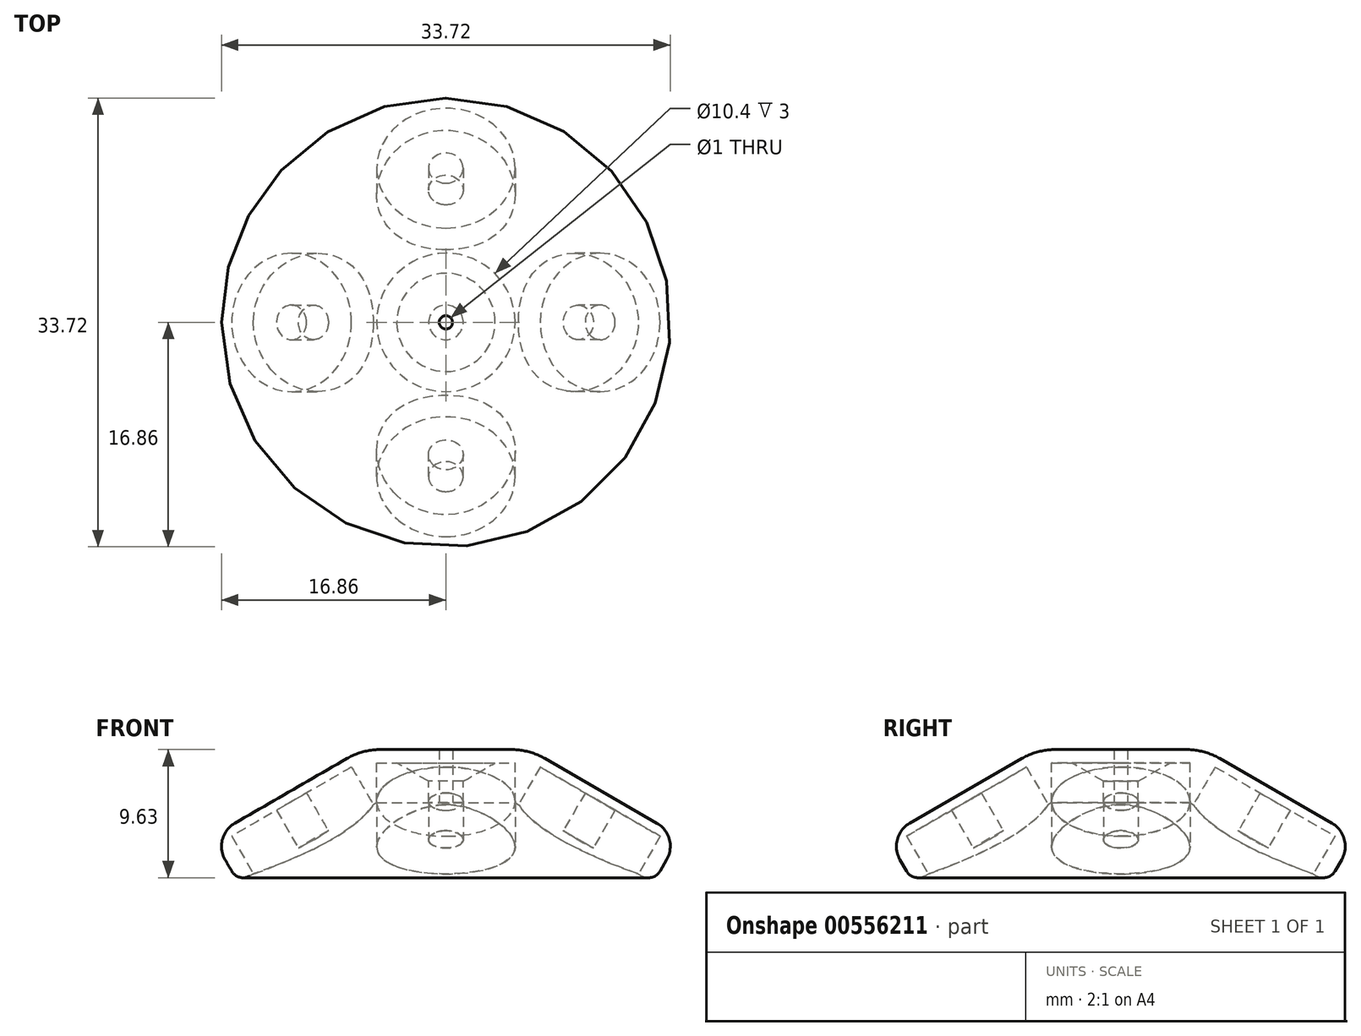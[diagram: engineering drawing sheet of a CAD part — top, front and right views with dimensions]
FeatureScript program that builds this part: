
annotation { "Feature Type Name" : "Feature", "Feature Type Description" : "" }
export const myFeature = defineFeature(function(context is Context, id is Id, definition is map)
    precondition{}
    {
        {
            var Q0;
            Q0=qCreatedBy(makeId("Top.planeOp"),FACE);
            var sketch = newSketch(context, id + "F0", { "sketchPlane" : qUnion([Q0])});
            skCircle(sketch, "E0", {"center": v(0, 0) * mm, "radius": 5 * mm});
            skSolve(sketch);
        }
        {
            var Q0;
            Q0=makeQuery(id+"F0.imprint","IMPRINT",FACE,{"disambiguationData":[TD([[makeQuery(id+"F0.imprint","IMPRINT",EDGE,{"derivedFrom":sQuery(id+"F0.wireOp",EDGE,"E0")}),1.0]])]});
            extrude(context, id + "F1", {"entities" : qUnion([Q0]), "depth" : 2.8 * mm, "offsetDistance" : 25 * mm});
        }
        {
            var Q0;
            Q0=sQuery(id+"F0.wireOp",VERTEX,"E0.center");
            var Q1;
            Q1=makeQuery(id+"F1.opExtrude","SWEPT_BODY",BODY,{"disambiguationData":[OSD([sQuery(id+"F0.wireOp",EDGE,"E0")])]});
            hole(context, id + "F2", {"style" : HoleStyle.C_SINK, "endStyle" : HoleEndStyle.THROUGH, "oppositeDirection" : true, "holeDiameter" : 3 * mm, "cSinkDiameter" : 7.5 * mm, "cSinkAngle" : 120 * degree, "isTappedThrough" : true, "tappedDepth" : 12 * mm, "tapClearance" : 3, "locations" : qUnion([Q0]), "scope" : qUnion([Q1])});
        }
        {
            var Q0;
            Q0=qCreatedBy(makeId("Front.planeOp"),FACE);
            var sketch = newSketch(context, id + "F3", { "sketchPlane" : qUnion([Q0])});
            skLineSegment(sketch, "E1", {"start": v(0, -16.53) * mm, "end": v(0, 20.94) * mm, "construction": true});
            skSolve(sketch);
        }
        {
            var Q0;
            Q0=qCreatedBy(makeId("Top.planeOp"),FACE);
            var sketch = newSketch(context, id + "F4", { "sketchPlane" : qUnion([Q0])});
            skLineSegment(sketch, "E2", {"start": v(0, -14.7) * mm, "end": v(0, 19.13) * mm, "construction": true});
            skSolve(sketch);
        }
        {
            var Q0;
            Q0=qCreatedBy(makeId("Top.planeOp"),FACE);
            var sketch = newSketch(context, id + "F5", { "sketchPlane" : qUnion([Q0])});
            skCircle(sketch, "E3", {"center": v(10.5, 0) * mm, "radius": 5 * mm});
            skLineSegment(sketch, "E4", {"start": v(-10.07, 0) * mm, "end": v(17.6, 0) * mm, "construction": true});
            skSolve(sketch);
        }
        {
            var Q0;
            Q0=makeQuery(id+"F5.imprint","IMPRINT",FACE,{"disambiguationData":[TD([[makeQuery(id+"F5.imprint","IMPRINT",EDGE,{"derivedFrom":sQuery(id+"F5.wireOp",EDGE,"E3")}),1.0]])]});
            extrude(context, id + "F6", {"entities" : qUnion([Q0]), "depth" : 4 * mm, "offsetDistance" : 25 * mm});
        }
        {
            var Q0;
            Q0=sQuery(id+"F5.wireOp",VERTEX,"E3.center");
            var Q1;
            Q1=makeQuery(id+"F6.opExtrude","SWEPT_BODY",BODY,{"disambiguationData":[OSD([sQuery(id+"F5.wireOp",EDGE,"E3")])]});
            hole(context, id + "F7", {"style" : HoleStyle.SIMPLE, "endStyle" : HoleEndStyle.THROUGH, "oppositeDirection" : true, "holeDiameter" : 3 * mm, "isTappedThrough" : true, "tappedDepth" : 12 * mm, "tapClearance" : 3, "locations" : qUnion([Q0]), "scope" : qUnion([Q1])});
        }
        {
            var Q0;
            Q0=makeQuery(id+"F6.opExtrude","SWEPT_BODY",BODY,{"disambiguationData":[OSD([sQuery(id+"F5.wireOp",EDGE,"E3")])]});
            var Q1;
            Q1=sQuery(id+"F4.wireOp",EDGE,"E2");
            var Q2;
            Q2=sQuery(id+"F4.wireOp",EDGE,"E2");
            transform(context, id + "F8", {"entities" : qUnion([Q0]), "transformType" : TransformType.ROTATION, "transformAxis" : qUnion([Q2]), "angle" : 30 * degree, "makeCopy" : false});
        }
        {
            var Q0;
            Q0=makeQuery(id+"F6.opExtrude","SWEPT_BODY",BODY,{"disambiguationData":[OSD([sQuery(id+"F5.wireOp",EDGE,"E3")])]});
            transform(context, id + "F9", {"entities" : qUnion([Q0]), "transformType" : TransformType.TRANSLATION_3D, "dx" : 0.4 * mm, "dy" : 0 * mm, "dz" : 1.7 * mm, "makeCopy" : false});
        }
        {
            var Q0;
            Q0=makeQuery(id+"F1.opExtrude","SWEPT_BODY",BODY,{"disambiguationData":[OSD([sQuery(id+"F0.wireOp",EDGE,"E0")])]});
            var Q1;
            Q1=sQuery(id+"F4.wireOp",EDGE,"E2");
            transform(context, id + "F10", {"entities" : qUnion([Q0]), "transformType" : TransformType.ROTATION, "transformAxis" : qUnion([Q1]), "angle" : 180 * degree, "makeCopy" : false});
        }
        {
            var Q0;
            Q0=makeQuery(id+"F1.opExtrude","SWEPT_BODY",BODY,{"disambiguationData":[OSD([sQuery(id+"F0.wireOp",EDGE,"E0")])]});
            transform(context, id + "F11", {"entities" : qUnion([Q0]), "transformType" : TransformType.TRANSLATION_3D, "dx" : 0 * mm, "dy" : 0 * mm, "dz" : 2.8 * mm, "makeCopy" : false});
        }
        {
            var Q0;
            Q0=makeQuery(id+"F6.opExtrude","SWEPT_BODY",BODY,{"disambiguationData":[OSD([sQuery(id+"F5.wireOp",EDGE,"E3")])]});
            var Q1;
            Q1=sQuery(id+"F3.wireOp",EDGE,"E1");
            circularPattern(context, id + "F12", {"entities" : qUnion([Q0]), "axis" : qUnion([Q1]), "angle" : 360 * degree, "instanceCount" : 4, "equalSpace" : true});
        }
        {
            var Q0;
            Q0=qCreatedBy(makeId("Front.planeOp"),FACE);
            var sketch = newSketch(context, id + "F13", { "sketchPlane" : qUnion([Q0])});
            skLineSegment(sketch, "E5", {"start": v(0, 0) * mm, "end": v(0, 4) * mm});
            skLineSegment(sketch, "E6", {"start": v(0, 4) * mm, "end": v(4.93, 4) * mm});
            skLineSegment(sketch, "E7", {"start": v(7.43, 3.33) * mm, "end": v(15.86, -1.54) * mm});
            skLineSegment(sketch, "E8", {"start": v(16.6, -4.27) * mm, "end": v(16.1, -5.13) * mm});
            skLineSegment(sketch, "E9", {"start": v(14.73, -5.5) * mm, "end": v(5.2, 0) * mm});
            skLineSegment(sketch, "E10", {"start": v(5.2, 0) * mm, "end": v(0, 0) * mm});
            skPoint(sketch, "E11.visualSharp", {"position": v(6.27, 4) * mm});
            skArc(sketch, "E11.filletArc", {"start": v(7.43, 3.33) * mm, "mid": v(6.23, 3.83) * mm, "end": v(4.93, 4) * mm});
            skPoint(sketch, "E12.visualSharp", {"position": v(17.6, -2.54) * mm});
            skArc(sketch, "E12.filletArc", {"start": v(16.6, -4.27) * mm, "mid": v(16.8, -2.75) * mm, "end": v(15.86, -1.54) * mm});
            skPoint(sketch, "E13.visualSharp", {"position": v(15.6, -6) * mm});
            skArc(sketch, "E13.filletArc", {"start": v(14.73, -5.5) * mm, "mid": v(15.49, -5.6) * mm, "end": v(16.1, -5.13) * mm});
            skSolve(sketch);
        }
        {
            var Q0;
            Q0 = qSketchRegion(id + "F13", true);
            var Q1;
            Q1=sQuery(id+"F3.wireOp",EDGE,"E1");
            revolve(context, id + "F14", {"entities" : qUnion([Q0]), "axis" : qUnion([Q1]), "revolveType" : RevolveType.FULL});
        }
        {
            var Q0;
            Q0=makeQuery(id+"F1.opExtrude","SWEPT_BODY",BODY,{"disambiguationData":[OSD([sQuery(id+"F0.wireOp",EDGE,"E0")])]});
            var Q1;
            Q1=makeQuery(id+"F6.opExtrude","SWEPT_BODY",BODY,{"disambiguationData":[OSD([sQuery(id+"F5.wireOp",EDGE,"E3")])]});
            var Q2;
            Q2=makeQuery(id+"F12.opPattern","COPY",BODY,{"derivedFrom":makeQuery(id+"F6.opExtrude","SWEPT_BODY",BODY,{"disambiguationData":[OSD([sQuery(id+"F5.wireOp",EDGE,"E3")])]}),"instanceName":"2"});
            var Q3;
            Q3=makeQuery(id+"F12.opPattern","COPY",BODY,{"derivedFrom":makeQuery(id+"F6.opExtrude","SWEPT_BODY",BODY,{"disambiguationData":[OSD([sQuery(id+"F5.wireOp",EDGE,"E3")])]}),"instanceName":"1"});
            var Q4;
            Q4=makeQuery(id+"F12.opPattern","COPY",BODY,{"derivedFrom":makeQuery(id+"F6.opExtrude","SWEPT_BODY",BODY,{"disambiguationData":[OSD([sQuery(id+"F5.wireOp",EDGE,"E3")])]}),"instanceName":"3"});
            var Q5;
            Q5=makeQuery(id+"F14.opRevolve","SWEPT_BODY",BODY,{"disambiguationData":[OSD([sQuery(id+"F13.wireOp",EDGE,"E5"),sQuery(id+"F13.wireOp",EDGE,"E6"),sQuery(id+"F13.wireOp",EDGE,"E7"),sQuery(id+"F13.wireOp",EDGE,"E8"),sQuery(id+"F13.wireOp",EDGE,"E9"),sQuery(id+"F13.wireOp",EDGE,"E10"),sQuery(id+"F13.wireOp",EDGE,"E11.filletArc"),sQuery(id+"F13.wireOp",EDGE,"E12.filletArc"),sQuery(id+"F13.wireOp",EDGE,"E13.filletArc")])]});
            booleanBodies(context, id + "F15", {"operationType" : BooleanOperationType.SUBTRACTION, "tools" : qUnion([Q0, Q1, Q2, Q3, Q4]), "targets" : qUnion([Q5]), "offset" : true, "offsetAll" : true, "offsetDistance" : 0.2 * mm});
        }
        {
            var Q0;
            Q0=sQuery(id+"F0.wireOp",VERTEX,"E0.center");
            var Q1;
            Q1=makeQuery(id+"F14.opRevolve","SWEPT_BODY",BODY,{"disambiguationData":[OSD([sQuery(id+"F13.wireOp",EDGE,"E5"),sQuery(id+"F13.wireOp",EDGE,"E6"),sQuery(id+"F13.wireOp",EDGE,"E7"),sQuery(id+"F13.wireOp",EDGE,"E8"),sQuery(id+"F13.wireOp",EDGE,"E9"),sQuery(id+"F13.wireOp",EDGE,"E10"),sQuery(id+"F13.wireOp",EDGE,"E11.filletArc"),sQuery(id+"F13.wireOp",EDGE,"E12.filletArc"),sQuery(id+"F13.wireOp",EDGE,"E13.filletArc")])]});
            hole(context, id + "F16", {"style" : HoleStyle.SIMPLE, "endStyle" : HoleEndStyle.THROUGH, "oppositeDirection" : true, "holeDiameter" : 1 * mm, "isTappedThrough" : true, "tappedDepth" : 12 * mm, "tapClearance" : 3, "locations" : qUnion([Q0]), "scope" : qUnion([Q1])});
        }
    });
